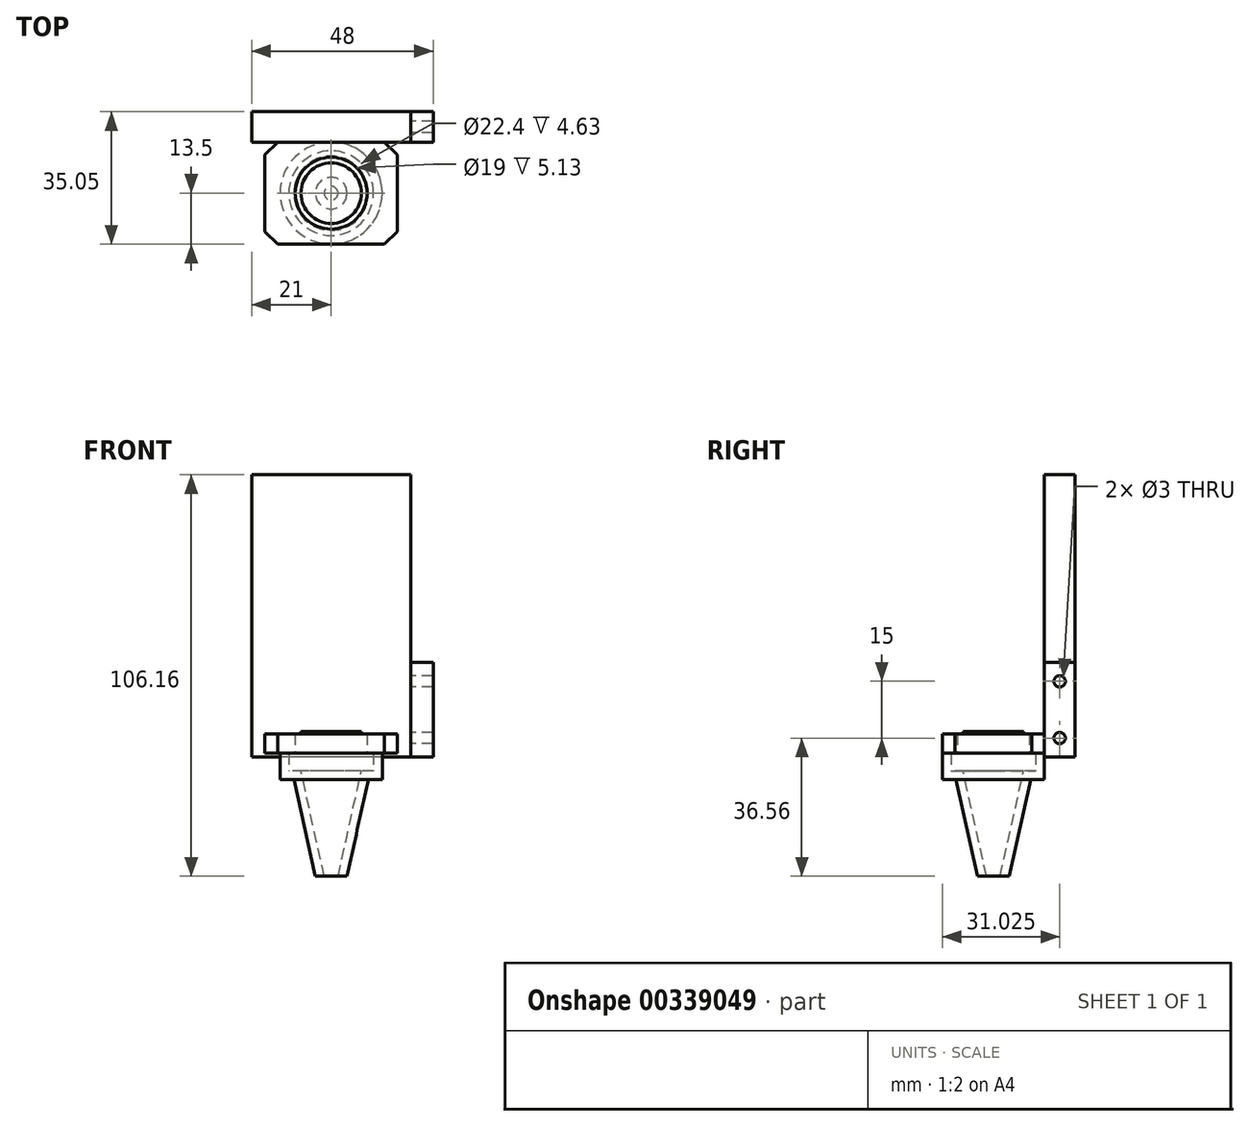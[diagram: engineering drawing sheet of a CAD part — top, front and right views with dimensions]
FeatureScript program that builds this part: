
annotation { "Feature Type Name" : "Feature", "Feature Type Description" : "" }
export const myFeature = defineFeature(function(context is Context, id is Id, definition is map)
    precondition{}
    {
        {
            var Q0;
            Q0=qCreatedBy(makeId("Top.planeOp"),FACE);
            var sketch = newSketch(context, id + "F0", { "sketchPlane" : qUnion([Q0])});
            skCircle(sketch, "E0", {"center": v(0, 0) * mm, "radius": 4.18 * mm});
            skSolve(sketch);
        }
        {
            var Q0;
            Q0=qCreatedBy(makeId("Top.planeOp"),FACE);
            cPlane(context, id + "F1", {"entities" : qUnion([Q0]), "cplaneType" : CPlaneType.OFFSET, "offset" : 25.6 * mm, "width" : 150 * mm, "height" : 150 * mm});
        }
        {
            var Q0;
            Q0=qCreatedBy(id+"F1.planeOp",FACE);
            var sketch = newSketch(context, id + "F2", { "sketchPlane" : qUnion([Q0])});
            skCircle(sketch, "E1", {"center": v(0, 0) * mm, "radius": 9.85 * mm});
            skCircle(sketch, "E2", {"center": v(0, 0) * mm, "radius": 13.5 * mm});
            skSolve(sketch);
        }
        {
            var Q0;
            Q0=makeQuery(id+"F2.imprint","IMPRINT",FACE,{"disambiguationData":[TD([[makeQuery(id+"F2.imprint","IMPRINT",EDGE,{"derivedFrom":sQuery(id+"F2.wireOp",EDGE,"E1")}),1.0]])]});
            var Q1;
            Q1=makeQuery(id+"F0.imprint","IMPRINT",FACE,{"disambiguationData":[TD([[makeQuery(id+"F0.imprint","IMPRINT",EDGE,{"derivedFrom":sQuery(id+"F0.wireOp",EDGE,"E0")}),1.0]])]});
            loft(context, id + "F3", {"sheetProfilesArray" : [{ "sheetProfileEntities" : qUnion([Q0]) }, { "sheetProfileEntities" : qUnion([Q1]) }]});
        }
        {
            var Q0;
            Q0=makeQuery(id+"F2.imprint","IMPRINT",FACE,{"disambiguationData":[TD([[makeQuery(id+"F2.imprint","IMPRINT",EDGE,{"derivedFrom":sQuery(id+"F2.wireOp",EDGE,"E1")}),-1.0]])]});
            var Q1;
            Q1=makeQuery(id+"F2.imprint","IMPRINT",FACE,{"disambiguationData":[TD([[makeQuery(id+"F2.imprint","IMPRINT",EDGE,{"derivedFrom":sQuery(id+"F2.wireOp",EDGE,"E1")}),1.0]])]});
            extrude(context, id + "F4", {"entities" : qUnion([Q0, Q1]), "operationType" : NewBodyOperationType.ADD, "depth" : 6.93 * mm});
        }
        {
            var Q0;
            Q0=makeQuery(id+"F4.opExtrude","CAP_FACE",FACE,{"disambiguationData":[OSD([sQuery(id+"F2.wireOp",EDGE,"E2")])],"isStart":false});
            var Q1;
            Q1=makeQuery(id+"F3.opLoft","CAP_FACE",FACE,{"disambiguationData":[OSD([makeQuery(id+"F0.imprint","IMPRINT",FACE,{"disambiguationData":[TD([[makeQuery(id+"F0.imprint","IMPRINT",EDGE,{"derivedFrom":sQuery(id+"F0.wireOp",EDGE,"E0")}),1.0]])]})])],"isStart":true});
            shell(context, id + "F5", {"entities" : qUnion([Q0, Q1]), "thickness" : 2.3 * mm});
        }
        {
            var Q0;
            Q0=makeQuery(id+"F4.opExtrude","CAP_FACE",FACE,{"disambiguationData":[OSD([sQuery(id+"F2.wireOp",EDGE,"E2")])],"isStart":false});
            var sketch = newSketch(context, id + "F6", { "sketchPlane" : qUnion([Q0])});
            skLineSegment(sketch, "E3.bottom", {"start": v(14.13, -13.5) * mm, "end": v(-14.13, -13.5) * mm});
            skLineSegment(sketch, "E3.top", {"start": v(14.13, 13.5) * mm, "end": v(-14.12, 13.5) * mm});
            skLineSegment(sketch, "E3.left", {"start": v(17.5, -10.13) * mm, "end": v(17.5, 10.12) * mm});
            skLineSegment(sketch, "E3.right", {"start": v(-17.5, -10.13) * mm, "end": v(-17.5, 10.12) * mm});
            skPoint(sketch, "E3.middle", {"position": v(0, 0) * mm});
            skCircle(sketch, "E4", {"center": v(0, 0) * mm, "radius": 10.7 * mm});
            skLineSegment(sketch, "E5", {"start": v(-14.13, 0) * mm, "end": v(14.13, 0) * mm, "construction": true});
            skLineSegment(sketch, "E6", {"start": v(-14.13, 13.5) * mm, "end": v(-14.13, -13.5) * mm, "construction": true});
            skLineSegment(sketch, "E7", {"start": v(14.13, 13.5) * mm, "end": v(14.13, -13.5) * mm, "construction": true});
            skLineSegment(sketch, "E8", {"start": v(-17.5, 10.12) * mm, "end": v(17.5, 10.12) * mm, "construction": true});
            skLineSegment(sketch, "E9", {"start": v(-17.5, -10.13) * mm, "end": v(17.5, -10.13) * mm, "construction": true});
            skLineSegment(sketch, "E10", {"start": v(-17.5, 10.12) * mm, "end": v(-14.13, 13.5) * mm});
            skLineSegment(sketch, "E11", {"start": v(14.13, 13.5) * mm, "end": v(17.5, 10.12) * mm});
            skLineSegment(sketch, "E12", {"start": v(14.13, -13.5) * mm, "end": v(17.5, -10.13) * mm});
            skLineSegment(sketch, "E13", {"start": v(-14.13, -13.5) * mm, "end": v(-17.5, -10.13) * mm});
            skPoint(sketch, "E14.orphan", {"position": v(-17.5, 13.5) * mm});
            skPoint(sketch, "E15.orphan", {"position": v(17.5, 13.5) * mm});
            skPoint(sketch, "E16.orphan", {"position": v(17.5, -13.5) * mm});
            skPoint(sketch, "E17.orphan", {"position": v(-17.5, -13.5) * mm});
            skCircle(sketch, "E18", {"center": v(0, 0) * mm, "radius": 9.5 * mm});
            skSolve(sketch);
        }
        {
            var Q0;
            Q0=makeQuery(id+"F6.imprint","IMPRINT",FACE,{"disambiguationData":[TD([[makeQuery(id+"F6.imprint","IMPRINT",EDGE,{"derivedFrom":sQuery(id+"F6.wireOp",EDGE,"E3.right")}),-1.0]])]});
            var Q1;
            Q1=makeQuery(id+"F6.imprint","IMPRINT",FACE,{"disambiguationData":[TD([[makeQuery(id+"F6.imprint","IMPRINT",EDGE,{"derivedFrom":sQuery(id+"F6.wireOp",EDGE,"E3.left")}),1.0]])]});
            var Q2;
            {var subQ0=sQuery(id+"F6.wireOp",EDGE,"E3.top");var subQ1=makeQuery(id+"F4.opExtrude","CAP_EDGE",EDGE,{"disambiguationData":[OSD([sQuery(id+"F2.wireOp",EDGE,"E2")])],"isStart":false});var subQ2=makeQuery(id+"F6.imprint","INTERSECT",VERTEX,{"disambiguationData":[OD(0.0)],"derivedFrom":[subQ1,subQ0]});Q2=makeQuery(id+"F6.imprint","IMPRINT",FACE,{"disambiguationData":[TD([[makeQuery(id+"F6.imprint","IMPRINT",EDGE,{"disambiguationData":[TD([[subQ2,-1.0]])],"derivedFrom":subQ0}),-1.0]])]});}
            var Q3;
            {var subQ0=sQuery(id+"F6.wireOp",EDGE,"E3.bottom");var subQ1=makeQuery(id+"F4.opExtrude","CAP_EDGE",EDGE,{"disambiguationData":[OSD([sQuery(id+"F2.wireOp",EDGE,"E2")])],"isStart":false});var subQ2=makeQuery(id+"F6.imprint","INTERSECT",VERTEX,{"disambiguationData":[OD(0.0)],"derivedFrom":[subQ1,subQ0]});Q3=makeQuery(id+"F6.imprint","IMPRINT",FACE,{"disambiguationData":[TD([[makeQuery(id+"F6.imprint","IMPRINT",EDGE,{"disambiguationData":[TD([[subQ2,-1.0]])],"derivedFrom":subQ0}),1.0]])]});}
            var Q4;
            {var subQ1=sQuery(id+"F2.wireOp",EDGE,"E2");var subQ2=makeQuery(id+"F4.opExtrude","CAP_EDGE",EDGE,{"disambiguationData":[OSD([subQ1])],"isStart":false});Q4=makeQuery(id+"F6.imprint","IMPRINT",FACE,{"disambiguationData":[TD([[makeQuery(id+"F6.imprint","IMPRINT",EDGE,{"derivedFrom":makeQuery(id+"F5.opShell","OFFSET_EDGE",EDGE,{"disambiguationData":[OSD([subQ1]),TDD([subQ2])]})}),-1.0]])]});}
            var Q5;
            Q5=makeQuery(id+"F6.imprint","IMPRINT",FACE,{"disambiguationData":[TD([[makeQuery(id+"F6.imprint","IMPRINT",EDGE,{"derivedFrom":sQuery(id+"F6.wireOp",EDGE,"E4")}),-1.0]])]});
            var Q6;
            Q6=makeQuery(id+"F6.imprint","IMPRINT",FACE,{"disambiguationData":[TD([[makeQuery(id+"F6.imprint","IMPRINT",EDGE,{"derivedFrom":sQuery(id+"F6.wireOp",EDGE,"E4")}),1.0]])]});
            extrude(context, id + "F7", {"entities" : qUnion([Q0, Q1, Q2, Q3, Q4, Q5, Q6]), "operationType" : NewBodyOperationType.ADD, "depth" : 5.13 * mm});
        }
        {
            var Q0;
            Q0=makeQuery(id+"F7.opExtrude","CAP_FACE",FACE,{"disambiguationData":[OSD([sQuery(id+"F2.wireOp",EDGE,"E2"),sQuery(id+"F6.wireOp",EDGE,"E3.bottom"),sQuery(id+"F6.wireOp",EDGE,"E3.top"),sQuery(id+"F6.wireOp",EDGE,"E3.left"),sQuery(id+"F6.wireOp",EDGE,"E3.right"),sQuery(id+"F6.wireOp",EDGE,"E4"),sQuery(id+"F6.wireOp",EDGE,"E10"),sQuery(id+"F6.wireOp",EDGE,"E11"),sQuery(id+"F6.wireOp",EDGE,"E12"),sQuery(id+"F6.wireOp",EDGE,"E13")])],"isStart":false});
            var sketch = newSketch(context, id + "F8", { "sketchPlane" : qUnion([Q0])});
            skCircle(sketch, "E19.0", {"center": v(0, 0) * mm, "radius": 9.85 * mm});
            skCircle(sketch, "E20.0", {"center": v(0, 0) * mm, "radius": 8 * mm});
            skSolve(sketch);
        }
        {
            var Q0;
            Q0=makeQuery(id+"F8.imprint","IMPRINT",FACE,{"disambiguationData":[TD([[makeQuery(id+"F8.imprint","IMPRINT",EDGE,{"derivedFrom":sQuery(id+"F8.wireOp",EDGE,"E20.0")}),1.0]])]});
            extrude(context, id + "F9", {"entities" : qUnion([Q0]), "depth" : .6 * mm});
        }
        {
            var Q0;
            Q0=makeQuery(id+"F7.opExtrude","CAP_FACE",FACE,{"disambiguationData":[OSD([sQuery(id+"F6.wireOp",EDGE,"E3.bottom"),sQuery(id+"F6.wireOp",EDGE,"E3.top"),sQuery(id+"F6.wireOp",EDGE,"E3.left"),sQuery(id+"F6.wireOp",EDGE,"E3.right"),sQuery(id+"F6.wireOp",EDGE,"E10"),sQuery(id+"F6.wireOp",EDGE,"E11"),sQuery(id+"F6.wireOp",EDGE,"E12"),sQuery(id+"F6.wireOp",EDGE,"E13"),sQuery(id+"F6.wireOp",EDGE,"E18")])],"isStart":false});
            var sketch = newSketch(context, id + "F10", { "sketchPlane" : qUnion([Q0])});
            skPoint(sketch, "E21.0", {"position": v(0, 13.5) * mm});
            skLineSegment(sketch, "E22.bottom", {"start": v(21, 13.5) * mm, "end": v(-21, 13.5) * mm});
            skLineSegment(sketch, "E22.top", {"start": v(21, 21.55) * mm, "end": v(-21, 21.55) * mm});
            skLineSegment(sketch, "E22.left", {"start": v(21, 13.5) * mm, "end": v(21, 21.55) * mm});
            skLineSegment(sketch, "E22.right", {"start": v(-21, 13.5) * mm, "end": v(-21, 21.55) * mm});
            skPoint(sketch, "E22.middle", {"position": v(0, 17.53) * mm});
            skSolve(sketch);
        }
        {
            var Q0;
            Q0=makeQuery(id+"F10.imprint","IMPRINT",FACE,{"disambiguationData":[TD([[makeQuery(id+"F10.imprint","IMPRINT",EDGE,{"derivedFrom":sQuery(id+"F10.wireOp",EDGE,"E22.top")}),1.0]])]});
            extrude(context, id + "F11", {"entities" : qUnion([Q0]), "depth" : 68.5 * mm, "hasSecondDirection" : true, "secondDirectionOppositeDirection" : true, "secondDirectionDepth" : 6.1 * mm});
        }
        {
            var Q0;
            Q0=makeQuery(id+"F11.opExtrude","SWEPT_FACE",FACE,{"disambiguationData":[OSD([sQuery(id+"F10.wireOp",EDGE,"E22.left")])]});
            var sketch = newSketch(context, id + "F12", { "sketchPlane" : qUnion([Q0])});
            skPoint(sketch, "E23.0", {"position": v(13.5, 31.56) * mm});
            skLineSegment(sketch, "E24.bottom", {"start": v(13.5, 31.56) * mm, "end": v(21.55, 31.56) * mm});
            skLineSegment(sketch, "E24.top", {"start": v(13.5, 56.56) * mm, "end": v(21.55, 56.56) * mm});
            skLineSegment(sketch, "E24.left", {"start": v(13.5, 31.56) * mm, "end": v(13.5, 56.56) * mm});
            skLineSegment(sketch, "E24.right", {"start": v(21.55, 31.56) * mm, "end": v(21.55, 56.56) * mm});
            skLineSegment(sketch, "E25", {"start": v(17.53, 56.56) * mm, "end": v(17.53, 51.56) * mm, "construction": true});
            skLineSegment(sketch, "E26", {"start": v(17.53, 31.56) * mm, "end": v(17.53, 36.56) * mm, "construction": true});
            skCircle(sketch, "E27", {"center": v(17.53, 36.56) * mm, "radius": 1.5 * mm});
            skCircle(sketch, "E28", {"center": v(17.53, 51.56) * mm, "radius": 1.5 * mm});
            skSolve(sketch);
        }
        {
            var Q0;
            Q0=makeQuery(id+"F12.imprint","IMPRINT",FACE,{"disambiguationData":[TD([[makeQuery(id+"F12.imprint","IMPRINT",EDGE,{"derivedFrom":sQuery(id+"F12.wireOp",EDGE,"E24.bottom")}),1.0]])]});
            extrude(context, id + "F13", {"entities" : qUnion([Q0]), "depth" : 6 * mm});
        }
    });
